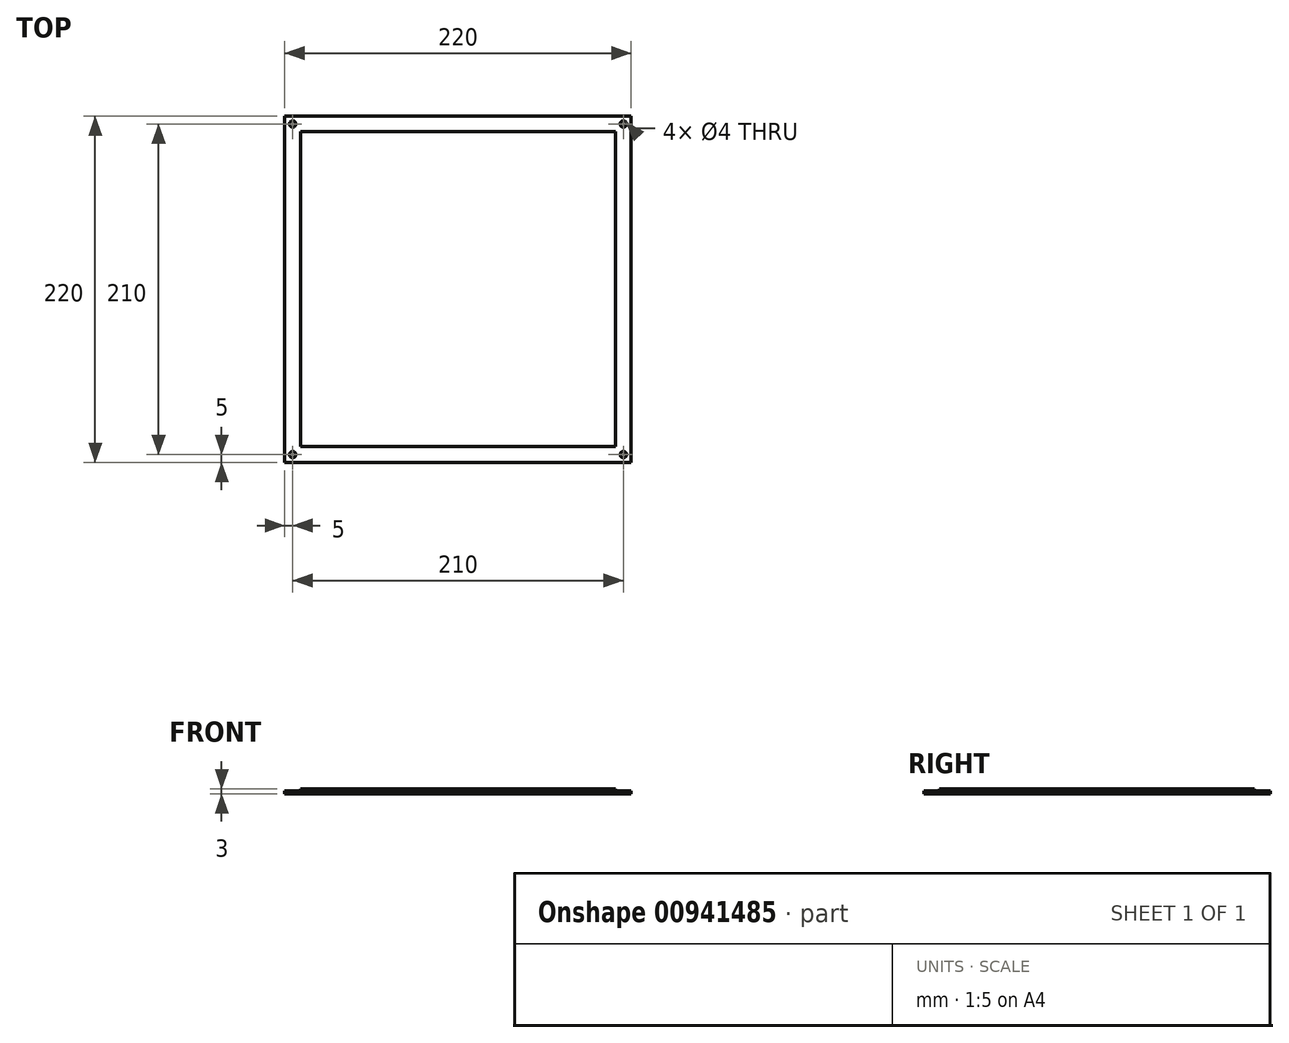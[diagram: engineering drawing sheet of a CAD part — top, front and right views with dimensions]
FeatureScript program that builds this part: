
annotation { "Feature Type Name" : "Feature", "Feature Type Description" : "" }
export const myFeature = defineFeature(function(context is Context, id is Id, definition is map)
    precondition{}
    {
        {
            var Q0;
            Q0=qCreatedBy(makeId("Top.planeOp"),FACE);
            var sketch = newSketch(context, id + "F0", { "sketchPlane" : qUnion([Q0])});
            skLineSegment(sketch, "E0.bottom", {"start": v(110, -110) * mm, "end": v(-110, -110) * mm});
            skLineSegment(sketch, "E0.top", {"start": v(110, 110) * mm, "end": v(-110, 110) * mm});
            skLineSegment(sketch, "E0.left", {"start": v(110, -110) * mm, "end": v(110, 110) * mm});
            skLineSegment(sketch, "E0.right", {"start": v(-110, -110) * mm, "end": v(-110, 110) * mm});
            skPoint(sketch, "E0.middle", {"position": v(0, 0) * mm});
            skSolve(sketch);
        }
        {
            var Q0;
            Q0=makeQuery(id+"F0.imprint","IMPRINT",FACE,{"disambiguationData":[TD([[makeQuery(id+"F0.imprint","IMPRINT",EDGE,{"derivedFrom":sQuery(id+"F0.wireOp",EDGE,"E0.bottom")}),-1.0]])]});
            extrude(context, id + "F1", {"entities" : qUnion([Q0]), "depth" : 2 * mm, "offsetDistance" : 25 * mm});
        }
        {
            var Q0;
            Q0=makeQuery(id+"F1.opExtrude","CAP_FACE",FACE,{"disambiguationData":[OSD([sQuery(id+"F0.wireOp",EDGE,"E0.bottom"),sQuery(id+"F0.wireOp",EDGE,"E0.top"),sQuery(id+"F0.wireOp",EDGE,"E0.left"),sQuery(id+"F0.wireOp",EDGE,"E0.right")])],"isStart":false});
            var sketch = newSketch(context, id + "F2", { "sketchPlane" : qUnion([Q0])});
            skCircle(sketch, "E1", {"center": v(-105, -105) * mm, "radius": 2 * mm});
            skCircle(sketch, "E2", {"center": v(105, -105) * mm, "radius": 2 * mm});
            skCircle(sketch, "E3", {"center": v(105, 105) * mm, "radius": 2 * mm});
            skCircle(sketch, "E4", {"center": v(-105, 105) * mm, "radius": 2 * mm});
            skSolve(sketch);
        }
        {
            var Q0;
            Q0=makeQuery(id+"F2.imprint","IMPRINT",FACE,{"disambiguationData":[TD([[makeQuery(id+"F2.imprint","IMPRINT",EDGE,{"derivedFrom":sQuery(id+"F2.wireOp",EDGE,"E1")}),1.0]])]});
            var Q1;
            Q1=makeQuery(id+"F2.imprint","IMPRINT",FACE,{"disambiguationData":[TD([[makeQuery(id+"F2.imprint","IMPRINT",EDGE,{"derivedFrom":sQuery(id+"F2.wireOp",EDGE,"E2")}),1.0]])]});
            var Q2;
            Q2=makeQuery(id+"F2.imprint","IMPRINT",FACE,{"disambiguationData":[TD([[makeQuery(id+"F2.imprint","IMPRINT",EDGE,{"derivedFrom":sQuery(id+"F2.wireOp",EDGE,"E3")}),1.0]])]});
            var Q3;
            Q3=makeQuery(id+"F2.imprint","IMPRINT",FACE,{"disambiguationData":[TD([[makeQuery(id+"F2.imprint","IMPRINT",EDGE,{"derivedFrom":sQuery(id+"F2.wireOp",EDGE,"E4")}),1.0]])]});
            extrude(context, id + "F3", {"entities" : qUnion([Q0, Q1, Q2, Q3]), "operationType" : NewBodyOperationType.REMOVE, "oppositeDirection" : true, "depth" : 25 * mm, "offsetDistance" : 25 * mm});
        }
        {
            var Q0;
            Q0=makeQuery(id+"F1.opExtrude","CAP_FACE",FACE,{"disambiguationData":[OSD([sQuery(id+"F0.wireOp",EDGE,"E0.bottom"),sQuery(id+"F0.wireOp",EDGE,"E0.top"),sQuery(id+"F0.wireOp",EDGE,"E0.left"),sQuery(id+"F0.wireOp",EDGE,"E0.right")])],"isStart":false});
            var sketch = newSketch(context, id + "F4", { "sketchPlane" : qUnion([Q0])});
            skLineSegment(sketch, "E5.bottom", {"start": v(100, -100) * mm, "end": v(-100, -100) * mm});
            skLineSegment(sketch, "E5.top", {"start": v(100, 100) * mm, "end": v(-100, 100) * mm});
            skLineSegment(sketch, "E5.left", {"start": v(100, -100) * mm, "end": v(100, 100) * mm});
            skLineSegment(sketch, "E5.right", {"start": v(-100, -100) * mm, "end": v(-100, 100) * mm});
            skPoint(sketch, "E5.middle", {"position": v(0, 0) * mm});
            skSolve(sketch);
        }
        {
            var Q0;
            Q0=makeQuery(id+"F4.imprint","IMPRINT",FACE,{"disambiguationData":[TD([[makeQuery(id+"F4.imprint","IMPRINT",EDGE,{"derivedFrom":sQuery(id+"F4.wireOp",EDGE,"E5.bottom")}),-1.0]])]});
            extrude(context, id + "F5", {"entities" : qUnion([Q0]), "operationType" : NewBodyOperationType.ADD, "depth" : 1 * mm, "offsetDistance" : 25 * mm});
        }
    });
